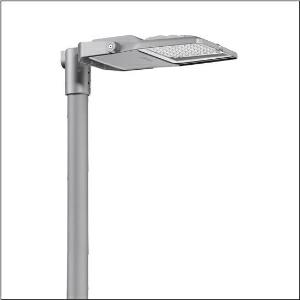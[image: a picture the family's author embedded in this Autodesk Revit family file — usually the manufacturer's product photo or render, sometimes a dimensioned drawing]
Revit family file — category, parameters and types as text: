
# Revit family: floodlight_fl_21_iq_mini___pl64_5xa7771d4e3a_aa37
name_source: partatom
category: Lighting Fixtures
units: mm (PartAtom-declared; Revit-internal decimal feet)

## family parameters
Cut with Voids When Loaded = No
Host = Face
Light Source = No
Part Type = Normal
Room Calculation Point = No
Round Connector Dimension = Use Diameter
Shared = No

## types (1)
- --- (1 x LED, 17970 lm, 143 W, 4000K)
    Apparent Load = 143 VA
    CIE Flux Codes = 28 80 98 100 100
    Color Rendering = 70
    Color Temperature = 4000K
    Default Elevation = 1800 mm
    Description = Floodlight FL 21 iQ mini, floodlight, primary light control with lens, of PMMA, primary optical cover: protective disc, of toughened safety glass, transparent, light distribution: PL64, light emission: direct distribution, installation type: surface-mounted, LED, High Power LED, rated luminous flux: 17.970lm, luminous efficacy: 126lm/W, light colour: 740, colour temperature: 4000K, control: Auto-Match, Temp-Guard, Lumen-Switch, Night-Set, Smart-Wire, Light-Fading, Desk-Remote (wireless, voltage-free reading and setting of iQ features in the workshop via application-optimized NFC function/RFID function), optimised constant luminous flux control (CLO 2.0), with terminal, 6-pole, mains connection: 220..240V, AC, 50/60Hz, start of lifetime: 143W, end of service life: 152W, reduction: 61W, luminaire housing, of diecast aluminium, powder-coated, Siteco® metallic grey (DB 702S), corrosivity category C5 mid according to DIN EN ISO 12944, sealing non-destructively replaceable, please order mast flange separately, mast bracket, of steel, galvanised, powder-coated, Siteco® metallic grey (DB 702S), protection rating (complete): IP66, insulation class (complete): insulation class II (safety insulation), certification: CE, ENEC, VDE, protection symbol: D, impact resistance: IK08, permissible operating ambient temperature: -40..+40°C, permissible operating ambient temperature for outdoor applications: -40..+50°C, standard: DIN EN 12944, LABS conformity tested according to VDMA 24364:2018-05, packaging unit: 1 piece

Light Distribution: PL64
    Height = 70 mm
    Lamp = 1 x LED
    Lamp Light Flux = 17970 lm
    Lamp Power = 143 W
    Lamp count = 1
    Length = 485 mm
    Luminous efficacy = 126 lm/W
    Manufacturer = Siteco
    ModVariant = No
    Model = 5XA7771D4E3A
    Number of Poles = 1
    OnlyDefault = Yes
    Power Factor = 1
    Product Name = Floodlight FL 21 iQ mini | PL64
    Product group = floodlight | pylon annexe
    ProductGroupID = 6200
    Protection Class = Protection class II
    Protection Degree = IP 66
    RLX_Detail_Level = 1
    RLX_Emergency_Light_Flux = 0 lm
    RLX_Emergency_Type = 0
    RLX_Emergency_Type_DB = No
    RlxData = <blob elided: 101557 chars, md5=8be4ab51>
    Socket = socket
    Standby Power = 0 W
    System Light Flux = 17970 lm
    System Power = 143 W
    Type Comments = factory setting: luminous flux: 100 % | dim-lin: 254 | 730 mA
    Type Image = l_1007125.jpg
    URL = http://relux.com
    VarID = @adj_116105
    Voltage = 0 V
    Weight = 0.00 kg
    Width = 337 mm

## geometry (parser evidence)
native form markers: Blend x4, Sweep x13
no freeform markers — native parametric forms only
